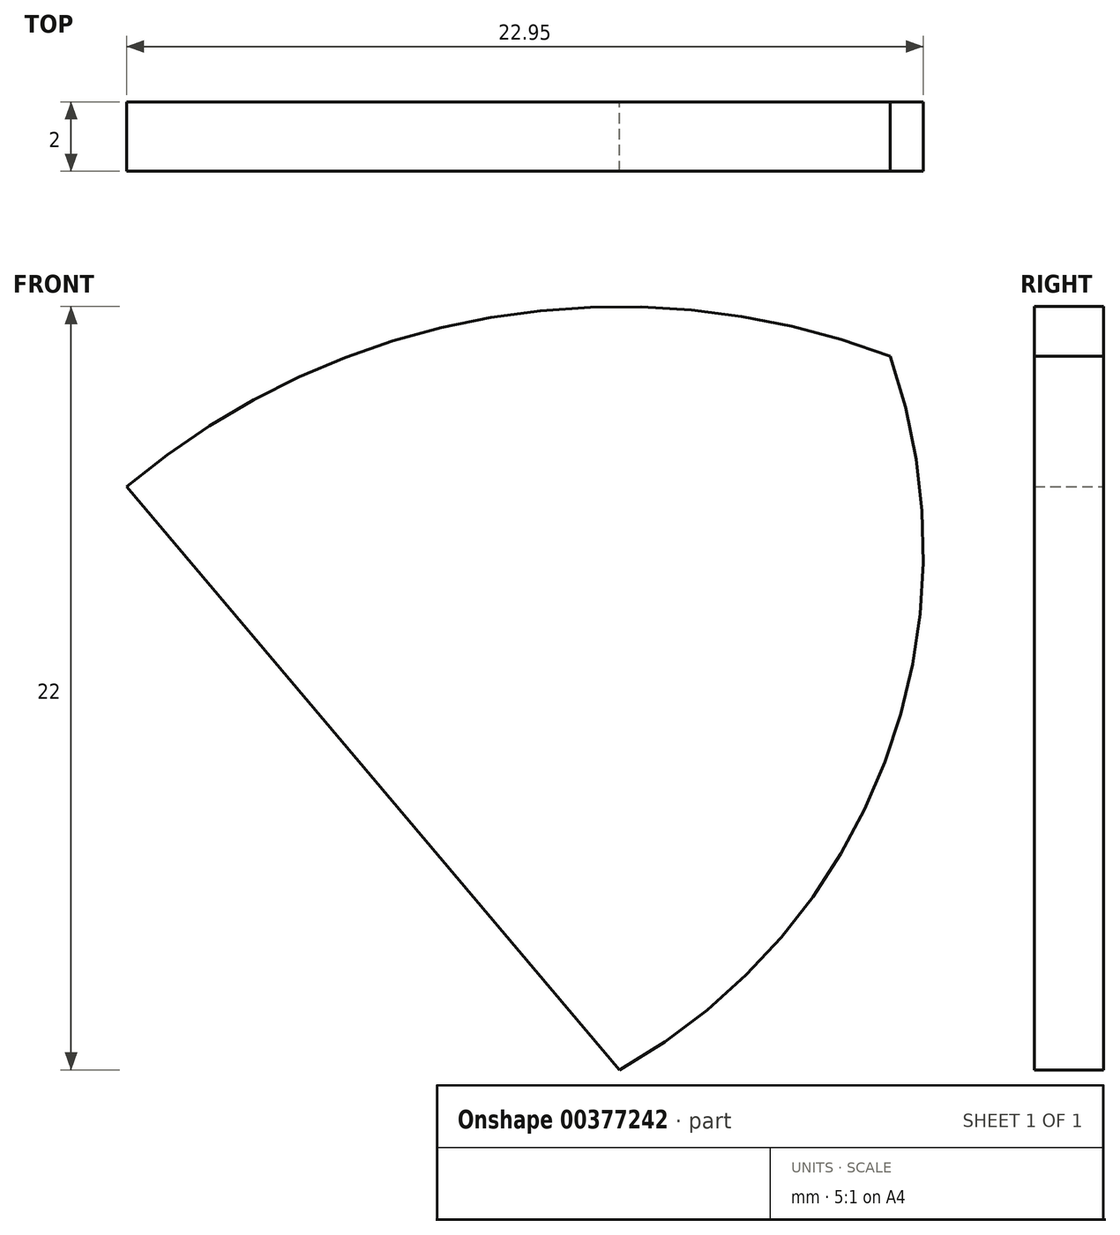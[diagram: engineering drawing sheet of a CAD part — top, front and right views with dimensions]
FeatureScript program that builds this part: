
annotation { "Feature Type Name" : "Feature", "Feature Type Description" : "" }
export const myFeature = defineFeature(function(context is Context, id is Id, definition is map)
    precondition{}
    {
        {
            var Q0;
            Q0=qCreatedBy(makeId("Front.planeOp"),FACE);
            var sketch = newSketch(context, id + "F0", { "sketchPlane" : qUnion([Q0])});
            skLineSegment(sketch, "E0", {"start": v(0, 0) * mm, "end": v(-14.2, 16.8) * mm});
            skArc(sketch, "E1", {"start": v(7.8, 20.57) * mm, "mid": v(-3.71, 21.68) * mm, "end": v(-14.2, 16.8) * mm});
            skLineSegment(sketch, "E2", {"start": v(0, 0) * mm, "end": v(7.8, 20.57) * mm, "construction": true});
            skArc(sketch, "E3", {"start": v(0, 0) * mm, "mid": v(7.64, 8.87) * mm, "end": v(7.8, 20.57) * mm});
            skSolve(sketch);
        }
        {
            var Q0;
            Q0=makeQuery(id+"F0.imprint","IMPRINT",FACE,{"disambiguationData":[TD([[makeQuery(id+"F0.imprint","IMPRINT",EDGE,{"derivedFrom":sQuery(id+"F0.wireOp",EDGE,"E0")}),-1.0]])]});
            extrude(context, id + "F1", {"entities" : qUnion([Q0]), "depth" : 2 * mm});
        }
    });
